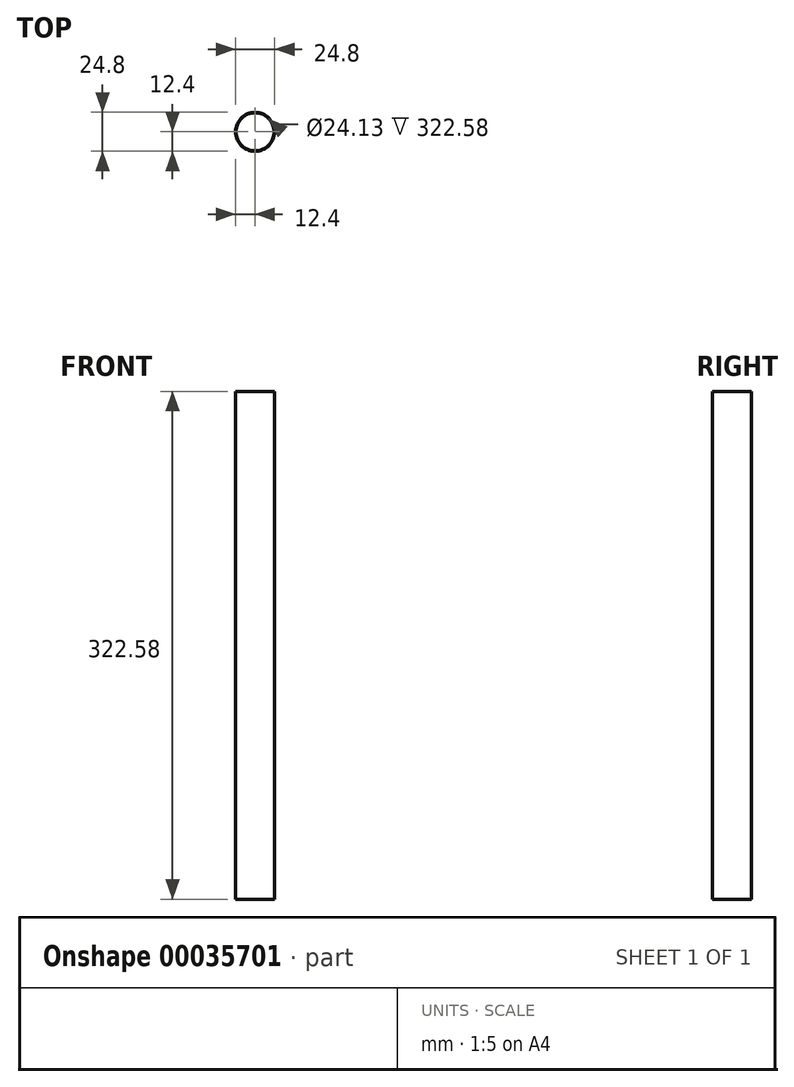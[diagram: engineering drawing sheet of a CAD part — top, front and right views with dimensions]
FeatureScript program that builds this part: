
annotation { "Feature Type Name" : "Feature", "Feature Type Description" : "" }
export const myFeature = defineFeature(function(context is Context, id is Id, definition is map)
    precondition{}
    {
        {
            var Q0;
            Q0=qCreatedBy(makeId("Front.planeOp"),FACE);
            var sketch = newSketch(context, id + "F0", { "sketchPlane" : qUnion([Q0])});
            skLineSegment(sketch, "E0", {"start": v(0, 0) * mm, "end": v(0, 322.58) * mm});
            skLineSegment(sketch, "E1", {"start": v(0, 322.58) * mm, "end": v(12.06, 322.58) * mm});
            skLineSegment(sketch, "E2", {"start": v(12.06, 322.58) * mm, "end": v(12.07, 0) * mm});
            skLineSegment(sketch, "E3", {"start": v(12.07, 0) * mm, "end": v(0, 0) * mm});
            skLineSegment(sketch, "E4", {"start": v(12.07, 0) * mm, "end": v(12.4, 0) * mm});
            skLineSegment(sketch, "E5", {"start": v(12.4, 0) * mm, "end": v(12.4, 322.58) * mm});
            skLineSegment(sketch, "E6", {"start": v(12.4, 322.58) * mm, "end": v(12.06, 322.58) * mm});
            skSolve(sketch);
        }
        {
            var Q0;
            Q0=makeQuery(id+"F0.imprint","IMPRINT",FACE,{"disambiguationData":[TD([[makeQuery(id+"F0.imprint","IMPRINT",EDGE,{"derivedFrom":sQuery(id+"F0.wireOp",EDGE,"E2")}),1.0]])]});
            var Q1;
            Q1=sQuery(id+"F0.wireOp",EDGE,"E0");
            revolve(context, id + "F1", {"entities" : qUnion([Q0]), "axis" : qUnion([Q1]), "revolveType" : RevolveType.FULL});
        }
    });
